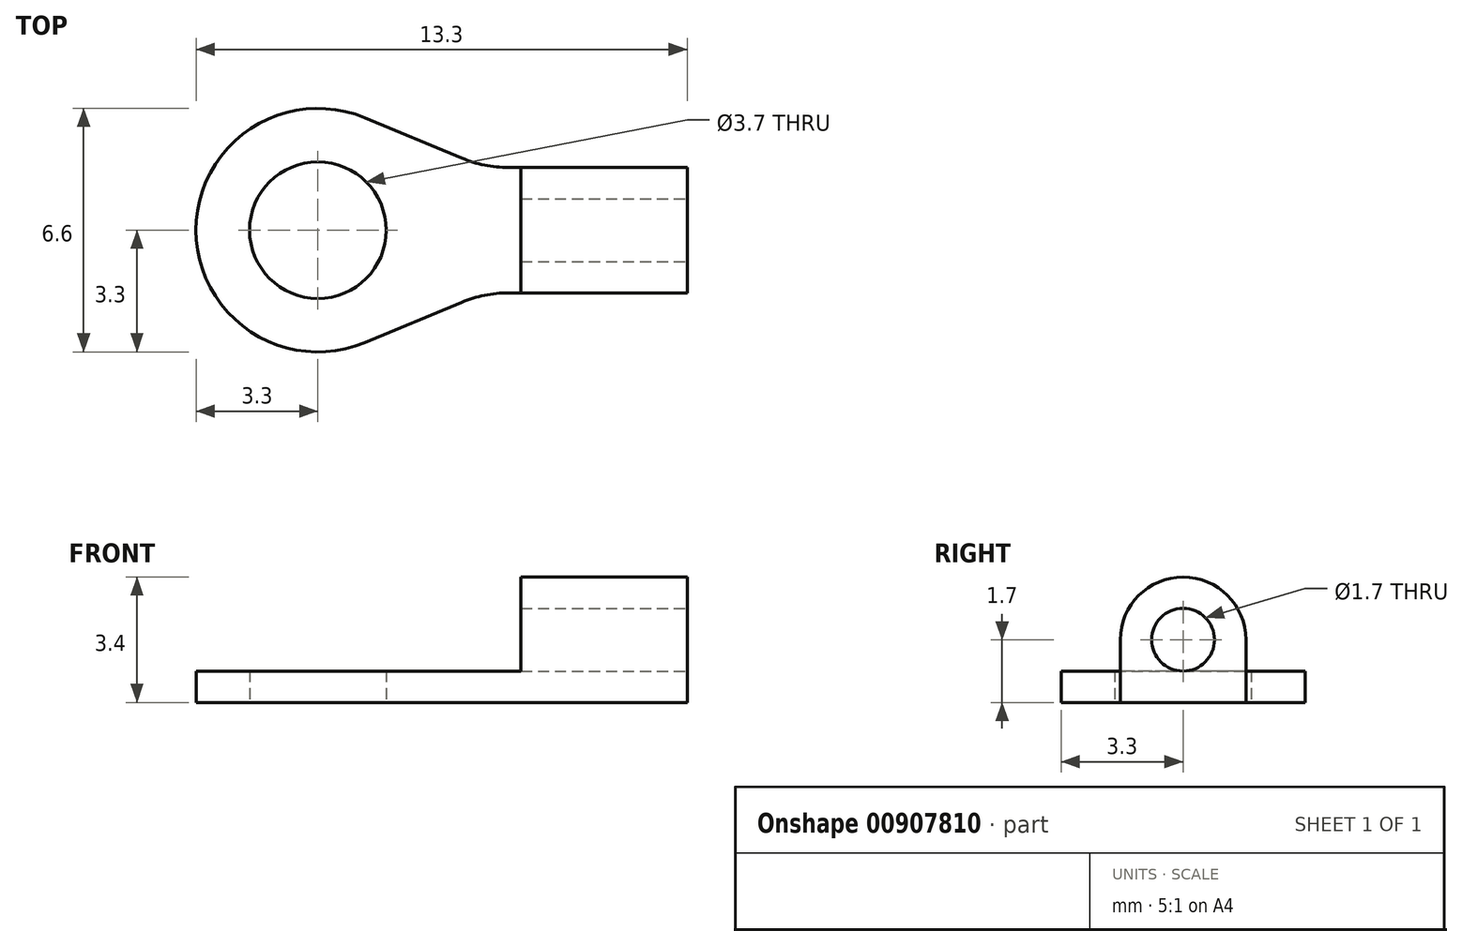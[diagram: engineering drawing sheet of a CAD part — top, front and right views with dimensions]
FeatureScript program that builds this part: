
annotation { "Feature Type Name" : "Feature", "Feature Type Description" : "" }
export const myFeature = defineFeature(function(context is Context, id is Id, definition is map)
    precondition{}
    {
        {
            var Q0;
            Q0=qCreatedBy(makeId("Top.planeOp"),FACE);
            var sketch = newSketch(context, id + "F0", { "sketchPlane" : qUnion([Q0])});
            skLineSegment(sketch, "E0.left", {"start": v(0, 3.3) * mm, "end": v(0, 3.3) * mm});
            skLineSegment(sketch, "E0.right", {"start": v(13.3, 1.6) * mm, "end": v(13.3, 5) * mm});
            skPoint(sketch, "E1.visualSharp", {"position": v(0, 6.6) * mm});
            skArc(sketch, "E1.filletArc", {"start": v(3.3, 6.6) * mm, "mid": v(0.97, 5.63) * mm, "end": v(0, 3.3) * mm});
            skPoint(sketch, "E2.visualSharp", {"position": v(0, 0) * mm});
            skArc(sketch, "E2.filletArc", {"start": v(0, 3.3) * mm, "mid": v(0.97, 0.97) * mm, "end": v(3.3, 0) * mm});
            skLineSegment(sketch, "E3.bottom", {"start": v(13.3, 1.6) * mm, "end": v(8.46, 1.6) * mm});
            skLineSegment(sketch, "E3.top", {"start": v(13.3, 5) * mm, "end": v(8.46, 5) * mm});
            skPoint(sketch, "E3.middle", {"position": v(13.3, 3.3) * mm});
            skArc(sketch, "E4", {"start": v(4.57, 6.35) * mm, "mid": v(0, 3.3) * mm, "end": v(4.57, 0.25) * mm});
            skCircle(sketch, "E5", {"center": v(3.3, 3.3) * mm, "radius": 1.85 * mm});
            skLineSegment(sketch, "E6", {"start": v(7.2, 5.25) * mm, "end": v(4.57, 6.35) * mm});
            skLineSegment(sketch, "E7", {"start": v(7.2, 1.35) * mm, "end": v(4.57, 0.25) * mm});
            skPoint(sketch, "E8.visualSharp", {"position": v(7.8, 5) * mm});
            skArc(sketch, "E8.filletArc", {"start": v(7.2, 5.25) * mm, "mid": v(7.81, 5.06) * mm, "end": v(8.46, 5) * mm});
            skPoint(sketch, "E9.visualSharp", {"position": v(7.8, 1.6) * mm});
            skArc(sketch, "E9.filletArc", {"start": v(8.46, 1.6) * mm, "mid": v(7.81, 1.54) * mm, "end": v(7.2, 1.35) * mm});
            skPoint(sketch, "E10.orphan", {"position": v(17.8, 5) * mm});
            skPoint(sketch, "E11.orphan", {"position": v(17.8, 1.6) * mm});
            skPoint(sketch, "E0.top.end.orphan", {"position": v(13.3, 6.6) * mm});
            skPoint(sketch, "E0.bottom.end.orphan", {"position": v(13.3, 0) * mm});
            skPoint(sketch, "E3.right.end.orphan", {"position": v(8.8, 5) * mm});
            skPoint(sketch, "E3.right.start.orphan", {"position": v(8.8, 1.6) * mm});
            skSolve(sketch);
        }
        {
            var Q0;
            Q0 = qSketchRegion(id + "F0", true);
            extrude(context, id + "F1", {"entities" : qUnion([Q0]), "depth" : 0.85 * mm, "offsetDistance" : 25 * mm});
        }
        {
            var Q0;
            Q0=makeQuery(id+"F1.opExtrude","CAP_FACE",FACE,{"disambiguationData":[OSD([sQuery(id+"F0.wireOp",EDGE,"E0.right"),sQuery(id+"F0.wireOp",EDGE,"E3.bottom"),sQuery(id+"F0.wireOp",EDGE,"E3.top"),sQuery(id+"F0.wireOp",EDGE,"E4"),sQuery(id+"F0.wireOp",EDGE,"E5"),sQuery(id+"F0.wireOp",EDGE,"E6"),sQuery(id+"F0.wireOp",EDGE,"E7"),sQuery(id+"F0.wireOp",EDGE,"E8.filletArc"),sQuery(id+"F0.wireOp",EDGE,"E9.filletArc")])],"isStart":false});
            var sketch = newSketch(context, id + "F2", { "sketchPlane" : qUnion([Q0])});
            skLineSegment(sketch, "E12.bottom", {"start": v(13.3, 5) * mm, "end": v(8.8, 5) * mm});
            skLineSegment(sketch, "E12.top", {"start": v(13.3, 1.6) * mm, "end": v(8.8, 1.6) * mm});
            skLineSegment(sketch, "E12.left", {"start": v(13.3, 5) * mm, "end": v(13.3, 1.6) * mm});
            skLineSegment(sketch, "E12.right", {"start": v(8.8, 5) * mm, "end": v(8.8, 1.6) * mm});
            skSolve(sketch);
        }
        {
            var Q0;
            Q0=makeQuery(id+"F2.imprint","IMPRINT",FACE,{"disambiguationData":[TD([[makeQuery(id+"F2.imprint","IMPRINT",EDGE,{"derivedFrom":sQuery(id+"F2.wireOp",EDGE,"E12.bottom")}),1.0]])]});
            extrude(context, id + "F3", {"entities" : qUnion([Q0]), "operationType" : NewBodyOperationType.ADD, "depth" : 2.55 * mm, "offsetDistance" : 25 * mm});
        }
        {
            var Q0;
            Q0=makeQuery(id+"F3.opExtrude","CAP_EDGE",EDGE,{"disambiguationData":[OSD([sQuery(id+"F2.wireOp",EDGE,"E12.bottom")])],"isStart":false});
            var Q1;
            Q1=makeQuery(id+"F3.opExtrude","CAP_EDGE",EDGE,{"disambiguationData":[OSD([sQuery(id+"F2.wireOp",EDGE,"E12.top")])],"isStart":false});
            fillet(context, id + "F4", {"entities" : qUnion([Q0, Q1]), "radius" : 1.7 * mm, "tangentPropagation" : true, "allowEdgeOverflow" : false});
        }
        {
            var Q0;
            Q0=makeQuery(id+"F3.boolean.opBoolean","MERGE",FACE,{"derivedFrom":[makeQuery(id+"F1.opExtrude","SWEPT_FACE",FACE,{"disambiguationData":[OSD([sQuery(id+"F0.wireOp",EDGE,"E0.right")])]}),makeQuery(id+"F3.opExtrude","SWEPT_FACE",FACE,{"disambiguationData":[OSD([sQuery(id+"F2.wireOp",EDGE,"E12.left")])]})]});
            var sketch = newSketch(context, id + "F5", { "sketchPlane" : qUnion([Q0])});
            skCircle(sketch, "E13", {"center": v(3.3, 1.7) * mm, "radius": 0.85 * mm});
            skSolve(sketch);
        }
        {
            var Q0;
            Q0=makeQuery(id+"F5.imprint","IMPRINT",FACE,{"disambiguationData":[TD([[makeQuery(id+"F5.imprint","IMPRINT",EDGE,{"derivedFrom":sQuery(id+"F5.wireOp",EDGE,"E13")}),1.0]])]});
            extrude(context, id + "F6", {"entities" : qUnion([Q0]), "operationType" : NewBodyOperationType.REMOVE, "oppositeDirection" : true, "depth" : 25 * mm, "offsetDistance" : 25 * mm});
        }
    });
